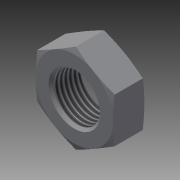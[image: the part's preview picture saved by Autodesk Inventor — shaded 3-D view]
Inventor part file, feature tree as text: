
AUTODESK INVENTOR PART (.ipt)
format: ipt  version: 2014 SP2 (Build 180246200, 246)  size: 157,696 bytes
history: native  units: in
note: dims shown in document units (in); Inventor stores cm internally (conversion verified against a paired STEP export)
features: other x70, sketch x3, revolve x2, extrude x1, thread x1
ambient origin geometry x8: Origin, YZ Plane, XZ Plane, XY Plane, X Axis, Y Axis, Z Axis, Center Point
bodies: Solid1 (feature_tree)
feature tree (77):
  sketch  "Sketch_8"  dims[d0=360.0deg d1=0.38in d2=0.0in]
  sketch  "Sketch_10"  dims[d3=360.0deg d4=0.3199in d5=0.0in]
  revolve  "Revolution1"  [1 undecoded]
  extrude  "Extrusion1"  Depth=0.3199in TaperAngle=0.0deg
  revolve  "Revolution2"  [1 undecoded]
  thread  "Thread1"  [1 undecoded]
  other  "NUT_XY"
  other  "NUT_YZ"
  other  "NUT_ZX"
  other  "NUT_X"
  other  "NUT_Y"
  other  "NUT_Z"
  other  "NUT_Center"
  other  "a1_XY"
  other  "a1_YZ"
  other  "a1_ZX"
  other  "a1_X"
  other  "a1_Y"
  other  "a1_Z"
  other  "a1_Center"
  other  "a2_XY"
  other  "a2_YZ"
  other  "a2_ZX"
  other  "a2_X"
  other  "a2_Y"
  other  "a2_Z"
  other  "a2_Center"
  other  "b1_XY"
  other  "b1_YZ"
  other  "b1_ZX"
  other  "b1_X"
  other  "b1_Y"
  other  "b1_Z"
  other  "b1_Center"
  other  "b2_XY"
  other  "b2_YZ"
  other  "b2_ZX"
  other  "b2_X"
  other  "b2_Y"
  other  "b2_Z"
  other  "b2_Center"
  other  "e_XY"
  other  "e_YZ"
  other  "e_ZX"
  other  "e_X"
  other  "e_Y"
  other  "e_Z"
  other  "e_Center"
  other  "ol1_XY"
  other  "ol1_YZ"
  other  "ol1_ZX"
  other  "ol1_X"
  other  "ol1_Y"
  other  "ol1_Z"
  other  "ol1_Center"
  other  "ol2_XY"
  other  "ol2_YZ"
  other  "ol2_ZX"
  other  "ol2_X"
  other  "ol2_Y"
  other  "ol2_Z"
  other  "ol2_Center"
  other  "th1_XY"
  other  "th1_YZ"
  other  "th1_ZX"
  other  "th1_X"
  other  "th1_Y"
  other  "th1_Z"
  other  "th1_Center"
  other  "th2_XY"
  other  "th2_YZ"
  other  "th2_ZX"
  other  "th2_X"
  other  "th2_Y"
  other  "th2_Z"
  other  "th2_Center"
  sketch  "Sketch_11"  dims[d6=0.0in d7=0.0in d8=0.0in]
note: 3 required parameter values undecoded (feature->parameter linkage not recoverable at this tier; creation-order binding heuristic only, values carry confidence <= 0.55)